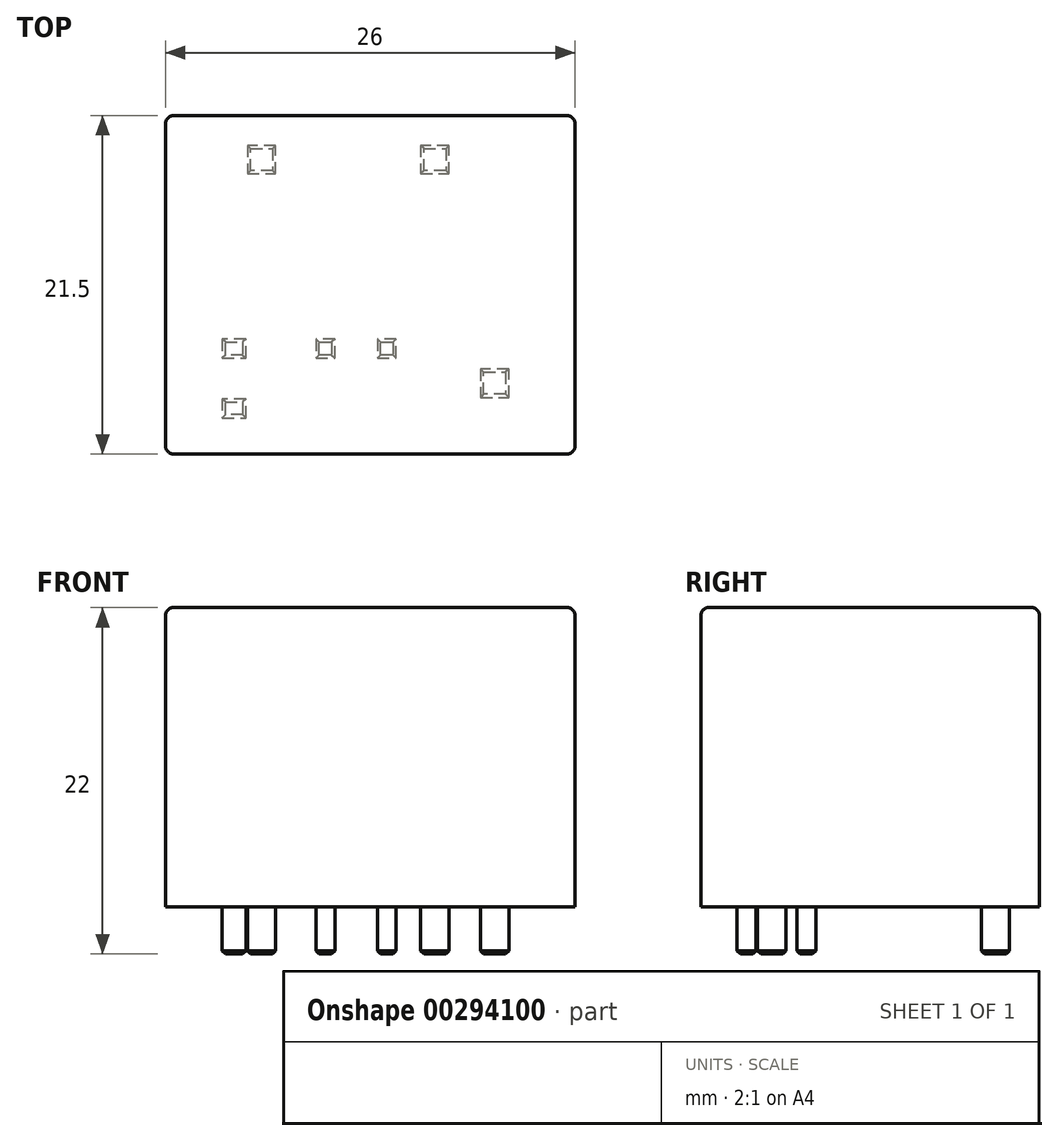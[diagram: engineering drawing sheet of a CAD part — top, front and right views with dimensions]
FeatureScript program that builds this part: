
annotation { "Feature Type Name" : "Feature", "Feature Type Description" : "" }
export const myFeature = defineFeature(function(context is Context, id is Id, definition is map)
    precondition{}
    {
        {
            var Q0;
            Q0=qCreatedBy(makeId("Top.planeOp"),FACE);
            var sketch = newSketch(context, id + "F0", { "sketchPlane" : qUnion([Q0])});
            skLineSegment(sketch, "E0.bottom", {"start": v(-13, -10.75) * mm, "end": v(13, -10.75) * mm});
            skLineSegment(sketch, "E0.top", {"start": v(-13, 10.75) * mm, "end": v(13, 10.75) * mm});
            skLineSegment(sketch, "E0.left", {"start": v(-13, -10.75) * mm, "end": v(-13, 10.75) * mm});
            skLineSegment(sketch, "E0.right", {"start": v(13, -10.75) * mm, "end": v(13, 10.75) * mm});
            skSolve(sketch);
        }
        {
            var Q0;
            Q0=qCreatedBy(makeId("Top.planeOp"),FACE);
            var sketch = newSketch(context, id + "F1", { "sketchPlane" : qUnion([Q0])});
            skLineSegment(sketch, "E1.bottom", {"start": v(-7.9, -3.45) * mm, "end": v(-9.4, -3.45) * mm});
            skLineSegment(sketch, "E1.top", {"start": v(-7.9, -4.65) * mm, "end": v(-9.4, -4.65) * mm});
            skLineSegment(sketch, "E1.left", {"start": v(-7.9, -3.45) * mm, "end": v(-7.9, -4.65) * mm});
            skLineSegment(sketch, "E1.right", {"start": v(-9.4, -3.45) * mm, "end": v(-9.4, -4.65) * mm});
            skPoint(sketch, "E1.middle", {"position": v(-8.65, -4.05) * mm});
            skLineSegment(sketch, "E2.bottom", {"start": v(-7.9, -7.25) * mm, "end": v(-9.4, -7.25) * mm});
            skLineSegment(sketch, "E2.top", {"start": v(-7.9, -8.45) * mm, "end": v(-9.4, -8.45) * mm});
            skLineSegment(sketch, "E2.left", {"start": v(-7.9, -7.25) * mm, "end": v(-7.9, -8.45) * mm});
            skLineSegment(sketch, "E2.right", {"start": v(-9.4, -7.25) * mm, "end": v(-9.4, -8.45) * mm});
            skPoint(sketch, "E2.middle", {"position": v(-8.65, -7.85) * mm});
            skLineSegment(sketch, "E3.bottom", {"start": v(-2.25, -3.45) * mm, "end": v(-3.45, -3.45) * mm});
            skLineSegment(sketch, "E3.top", {"start": v(-2.25, -4.65) * mm, "end": v(-3.45, -4.65) * mm});
            skLineSegment(sketch, "E3.left", {"start": v(-2.25, -3.45) * mm, "end": v(-2.25, -4.65) * mm});
            skLineSegment(sketch, "E3.right", {"start": v(-3.45, -3.45) * mm, "end": v(-3.45, -4.65) * mm});
            skPoint(sketch, "E3.middle", {"position": v(-2.85, -4.05) * mm});
            skLineSegment(sketch, "E4.bottom", {"start": v(1.65, -3.45) * mm, "end": v(0.45, -3.45) * mm});
            skLineSegment(sketch, "E4.top", {"start": v(1.65, -4.65) * mm, "end": v(0.45, -4.65) * mm});
            skLineSegment(sketch, "E4.left", {"start": v(1.65, -3.45) * mm, "end": v(1.65, -4.65) * mm});
            skLineSegment(sketch, "E4.right", {"start": v(0.45, -3.45) * mm, "end": v(0.45, -4.65) * mm});
            skPoint(sketch, "E4.middle", {"position": v(1.05, -4.05) * mm});
            skLineSegment(sketch, "E5.bottom", {"start": v(-6, 8.85) * mm, "end": v(-7.8, 8.85) * mm});
            skLineSegment(sketch, "E5.top", {"start": v(-6, 7.05) * mm, "end": v(-7.8, 7.05) * mm});
            skLineSegment(sketch, "E5.left", {"start": v(-6, 8.85) * mm, "end": v(-6, 7.05) * mm});
            skLineSegment(sketch, "E5.right", {"start": v(-7.8, 8.85) * mm, "end": v(-7.8, 7.05) * mm});
            skPoint(sketch, "E5.middle", {"position": v(-6.9, 7.95) * mm});
            skLineSegment(sketch, "E6.bottom", {"start": v(5, 8.85) * mm, "end": v(3.2, 8.85) * mm});
            skLineSegment(sketch, "E6.top", {"start": v(5, 7.05) * mm, "end": v(3.2, 7.05) * mm});
            skLineSegment(sketch, "E6.left", {"start": v(5, 8.85) * mm, "end": v(5, 7.05) * mm});
            skLineSegment(sketch, "E6.right", {"start": v(3.2, 8.85) * mm, "end": v(3.2, 7.05) * mm});
            skPoint(sketch, "E6.middle", {"position": v(4.1, 7.95) * mm});
            skLineSegment(sketch, "E7.bottom", {"start": v(8.8, -5.35) * mm, "end": v(7, -5.35) * mm});
            skLineSegment(sketch, "E7.top", {"start": v(8.8, -7.15) * mm, "end": v(7, -7.15) * mm});
            skLineSegment(sketch, "E7.left", {"start": v(8.8, -5.35) * mm, "end": v(8.8, -7.15) * mm});
            skLineSegment(sketch, "E7.right", {"start": v(7, -5.35) * mm, "end": v(7, -7.15) * mm});
            skPoint(sketch, "E7.middle", {"position": v(7.9, -6.25) * mm});
            skSolve(sketch);
        }
        {
            var Q0;
            Q0=makeQuery(id+"F0.imprint","IMPRINT",FACE,{"disambiguationData":[TD([[makeQuery(id+"F0.imprint","IMPRINT",EDGE,{"derivedFrom":sQuery(id+"F0.wireOp",EDGE,"E0.bottom")}),1.0]])]});
            extrude(context, id + "F2", {"entities" : qUnion([Q0]), "depth" : 19 * mm});
        }
        {
            var Q0;
            Q0=makeQuery(id+"F1.imprint","IMPRINT",FACE,{"disambiguationData":[TD([[makeQuery(id+"F1.imprint","IMPRINT",EDGE,{"derivedFrom":sQuery(id+"F1.wireOp",EDGE,"E6.bottom")}),1.0]])]});
            var Q1;
            Q1=makeQuery(id+"F1.imprint","IMPRINT",FACE,{"disambiguationData":[TD([[makeQuery(id+"F1.imprint","IMPRINT",EDGE,{"derivedFrom":sQuery(id+"F1.wireOp",EDGE,"E5.bottom")}),1.0]])]});
            var Q2;
            Q2=makeQuery(id+"F1.imprint","IMPRINT",FACE,{"disambiguationData":[TD([[makeQuery(id+"F1.imprint","IMPRINT",EDGE,{"derivedFrom":sQuery(id+"F1.wireOp",EDGE,"E1.bottom")}),1.0]])]});
            var Q3;
            Q3=makeQuery(id+"F1.imprint","IMPRINT",FACE,{"disambiguationData":[TD([[makeQuery(id+"F1.imprint","IMPRINT",EDGE,{"derivedFrom":sQuery(id+"F1.wireOp",EDGE,"E3.bottom")}),1.0]])]});
            var Q4;
            Q4=makeQuery(id+"F1.imprint","IMPRINT",FACE,{"disambiguationData":[TD([[makeQuery(id+"F1.imprint","IMPRINT",EDGE,{"derivedFrom":sQuery(id+"F1.wireOp",EDGE,"E4.bottom")}),1.0]])]});
            var Q5;
            Q5=makeQuery(id+"F1.imprint","IMPRINT",FACE,{"disambiguationData":[TD([[makeQuery(id+"F1.imprint","IMPRINT",EDGE,{"derivedFrom":sQuery(id+"F1.wireOp",EDGE,"E2.bottom")}),1.0]])]});
            var Q6;
            Q6=makeQuery(id+"F1.imprint","IMPRINT",FACE,{"disambiguationData":[TD([[makeQuery(id+"F1.imprint","IMPRINT",EDGE,{"derivedFrom":sQuery(id+"F1.wireOp",EDGE,"E7.bottom")}),1.0]])]});
            extrude(context, id + "F3", {"entities" : qUnion([Q0, Q1, Q2, Q3, Q4, Q5, Q6]), "oppositeDirection" : true, "depth" : 3 * mm});
        }
        {
            var Q0;
            Q0=makeQuery(id+"F2.opExtrude","SWEPT_EDGE",EDGE,{"disambiguationData":[OSD([sQuery(id+"F0.wireOp",EDGE,"E0.top"),sQuery(id+"F0.wireOp",EDGE,"E0.left")])]});
            var Q1;
            Q1=makeQuery(id+"F2.opExtrude","CAP_EDGE",EDGE,{"disambiguationData":[OSD([sQuery(id+"F0.wireOp",EDGE,"E0.left")])],"isStart":false});
            var Q2;
            Q2=makeQuery(id+"F2.opExtrude","CAP_EDGE",EDGE,{"disambiguationData":[OSD([sQuery(id+"F0.wireOp",EDGE,"E0.top")])],"isStart":false});
            var Q3;
            Q3=makeQuery(id+"F2.opExtrude","CAP_EDGE",EDGE,{"disambiguationData":[OSD([sQuery(id+"F0.wireOp",EDGE,"E0.bottom")])],"isStart":false});
            var Q4;
            Q4=makeQuery(id+"F2.opExtrude","SWEPT_EDGE",EDGE,{"disambiguationData":[OSD([sQuery(id+"F0.wireOp",EDGE,"E0.bottom"),sQuery(id+"F0.wireOp",EDGE,"E0.left")])]});
            var Q5;
            Q5=makeQuery(id+"F2.opExtrude","SWEPT_EDGE",EDGE,{"disambiguationData":[OSD([sQuery(id+"F0.wireOp",EDGE,"E0.top"),sQuery(id+"F0.wireOp",EDGE,"E0.right")])]});
            var Q6;
            Q6=makeQuery(id+"F2.opExtrude","SWEPT_EDGE",EDGE,{"disambiguationData":[OSD([sQuery(id+"F0.wireOp",EDGE,"E0.bottom"),sQuery(id+"F0.wireOp",EDGE,"E0.right")])]});
            var Q7;
            Q7=makeQuery(id+"F2.opExtrude","CAP_EDGE",EDGE,{"disambiguationData":[OSD([sQuery(id+"F0.wireOp",EDGE,"E0.right")])],"isStart":false});
            fillet(context, id + "F4", {"entities" : qUnion([Q0, Q1, Q2, Q3, Q4, Q5, Q6, Q7]), "radius" : 0.5 * mm, "tangentPropagation" : true, "allowEdgeOverflow" : false});
        }
        {
            var Q0;
            Q0=makeQuery(id+"F3.opExtrude","CAP_FACE",FACE,{"disambiguationData":[OSD([sQuery(id+"F1.wireOp",EDGE,"E6.bottom"),sQuery(id+"F1.wireOp",EDGE,"E6.top"),sQuery(id+"F1.wireOp",EDGE,"E6.left"),sQuery(id+"F1.wireOp",EDGE,"E6.right")])],"isStart":false});
            var Q1;
            Q1=makeQuery(id+"F3.opExtrude","CAP_FACE",FACE,{"disambiguationData":[OSD([sQuery(id+"F1.wireOp",EDGE,"E5.bottom"),sQuery(id+"F1.wireOp",EDGE,"E5.top"),sQuery(id+"F1.wireOp",EDGE,"E5.left"),sQuery(id+"F1.wireOp",EDGE,"E5.right")])],"isStart":false});
            var Q2;
            Q2=makeQuery(id+"F3.opExtrude","CAP_FACE",FACE,{"disambiguationData":[OSD([sQuery(id+"F1.wireOp",EDGE,"E7.bottom"),sQuery(id+"F1.wireOp",EDGE,"E7.top"),sQuery(id+"F1.wireOp",EDGE,"E7.left"),sQuery(id+"F1.wireOp",EDGE,"E7.right")])],"isStart":false});
            var Q3;
            Q3=makeQuery(id+"F3.opExtrude","CAP_FACE",FACE,{"disambiguationData":[OSD([sQuery(id+"F1.wireOp",EDGE,"E2.bottom"),sQuery(id+"F1.wireOp",EDGE,"E2.top"),sQuery(id+"F1.wireOp",EDGE,"E2.left"),sQuery(id+"F1.wireOp",EDGE,"E2.right")])],"isStart":false});
            var Q4;
            Q4=makeQuery(id+"F3.opExtrude","CAP_FACE",FACE,{"disambiguationData":[OSD([sQuery(id+"F1.wireOp",EDGE,"E1.bottom"),sQuery(id+"F1.wireOp",EDGE,"E1.top"),sQuery(id+"F1.wireOp",EDGE,"E1.left"),sQuery(id+"F1.wireOp",EDGE,"E1.right")])],"isStart":false});
            var Q5;
            Q5=makeQuery(id+"F3.opExtrude","CAP_FACE",FACE,{"disambiguationData":[OSD([sQuery(id+"F1.wireOp",EDGE,"E3.bottom"),sQuery(id+"F1.wireOp",EDGE,"E3.top"),sQuery(id+"F1.wireOp",EDGE,"E3.left"),sQuery(id+"F1.wireOp",EDGE,"E3.right")])],"isStart":false});
            var Q6;
            Q6=makeQuery(id+"F3.opExtrude","CAP_FACE",FACE,{"disambiguationData":[OSD([sQuery(id+"F1.wireOp",EDGE,"E4.bottom"),sQuery(id+"F1.wireOp",EDGE,"E4.top"),sQuery(id+"F1.wireOp",EDGE,"E4.left"),sQuery(id+"F1.wireOp",EDGE,"E4.right")])],"isStart":false});
            chamfer(context, id + "F5", {"entities" : qUnion([Q0, Q1, Q2, Q3, Q4, Q5, Q6]), "width" : 0.2 * mm, "tangentPropagation" : true});
        }
    });
